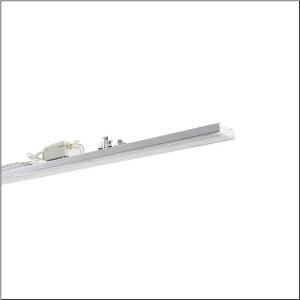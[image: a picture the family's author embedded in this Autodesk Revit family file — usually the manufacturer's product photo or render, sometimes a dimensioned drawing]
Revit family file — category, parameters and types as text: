
# Revit family: licross_21_recessed_ho_52tl12dn4fxmd
name_source: partatom
category: Lighting Fixtures
units: mm (PartAtom-declared; Revit-internal decimal feet)

## family parameters
Cut with Voids When Loaded = No
Host = Face
Light Source = No
Part Type = Normal
Room Calculation Point = No
Round Connector Dimension = Use Diameter
Shared = No

## types (1)
- --- (1 x LED, 2250 lm, 14 W, 4000K)
    Apparent Load = 14 VA
    CIE Flux Codes = 69 91 98 100 100
    Color Rendering = 80
    Color Temperature = 4000K
    Default Elevation = 1800 mm
    Description = Licross 21 Recessed HO, luminaire insert, of sheet steel, galvanised, coil coated, white, length: 1.500mm, width: 66mm, height: 67mm, LED rated luminous flux: 15.000lm, light colour: 840, SDCM (Standard Deviation of Colour Matching)MacAdam ≤ 3 SDCM (initial), control gear: DALI 2 (for two DALI lines), with plug, 6-pole, with phase selection, mains connection: 220..240V, AC/DC, 0/50..60Hz, rated input power: 85W, without changeover relay, for emergency light function, for central battery installations according to EN 60598-2-22, internal wiring halogen-free, primary optical cover: cover, of PMMA, light emission: direct distribution, primary light characteristic: symmetric, protection rating (complete): IP40, insulation class (complete): insulation class I (protective earthing), certification: CE, ENEC, VDE, UKCA, protection symbol: D if used in an environment without relevant dust loads with corresponding accessories, impact resistance: IK06, permissible ambient temperature for indoor applications: -25..+30°C, standard: EN 60598-2-22, corresponds to IFS (International Featured Standards) requirements for safety and quality in the food industry, reducing of maximum allowable ambient temperature of 5°C with ceiling mounting, LABS conformity tested according to VDMA 24364:2018-05, The light source and the operating device comply with the requirements of the Ecodesign Regulation (EU) 2019/2020 and are replaceable in accordance with this regulation, packaging unit: 1 piece
    Height = 58 mm
    Lamp = 1 x LED
    Lamp Light Flux = 2250 lm
    Lamp Power = 14 W
    Lamp count = 1
    Length = 1500 mm
    Luminous efficacy = 161 lm/W
    Manufacturer = Siteco
    ModVariant = No
    Model = 52TL12DN4FXMD
    Mounting Place = Ceiling
    Mounting Type = Pendant
    Number of Poles = 1
    OnlyDefault = Yes
    Power Factor = 1
    Product Name = Licross 21 Recessed HO
    Product group = luminaire insert | ceiling pendant
    ProductGroupID = 901
    Protection Class = Protection class I
    Protection Degree = IP 40
    RLX_Detail_Level = 1
    RLX_Emergency_Light_Flux = 0 lm
    RLX_Emergency_Type = 0
    RLX_Emergency_Type_DB = No
    RlxData = <blob elided: 25437 chars, md5=bb93733c>
    Socket = socket
    Standby Power = 0 W
    System Light Flux = 2250 lm
    System Power = 14 W
    Type Comments = : DC mode (central or group accumulator) initial emergency light level
    Type Image = l_1296930.jpg
    URL = http://relux.com
    VarID = @adj_113273
    Voltage = 0 V
    Weight = 0.00 kg
    Width = 66 mm

## geometry (parser evidence)
native form markers: Blend x4, Sweep x11
no freeform markers — native parametric forms only
